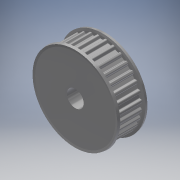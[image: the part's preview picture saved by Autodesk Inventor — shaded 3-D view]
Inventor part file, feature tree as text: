
AUTODESK INVENTOR PART (.ipt)
format: ipt  version: 2017 (Build 210142000, 142)  size: 486,400 bytes
history: native  units: mm (DEFAULTED — no unit token found)
features: other x3, extrude x2, fillet x1, pattern_circular x1, hole x1, sketch x1
ambient origin geometry x8: Origin, YZ Plane, XZ Plane, XY Plane, X Axis, Y Axis, Z Axis, Center Point
bodies: Solid1 (feature_tree)
feature tree (9):
  other  "Esquisse de poulie"
  extrude  "Corps de base"  Depth=25.464791mm
  extrude  "Dent"  Depth=0.3mm
  fillet  "Fillet"  Radius=0.75mm
  pattern_circular  "Dents"  [2 undecoded]
  other  "Bride gauche"
  other  "Bride droite"
  hole  "Perçage1"  [1 undecoded]
  sketch  "Esquisse2"
note: 3 required parameter values undecoded (feature->parameter linkage not recoverable at this tier; creation-order binding heuristic only, values carry confidence <= 0.55)
